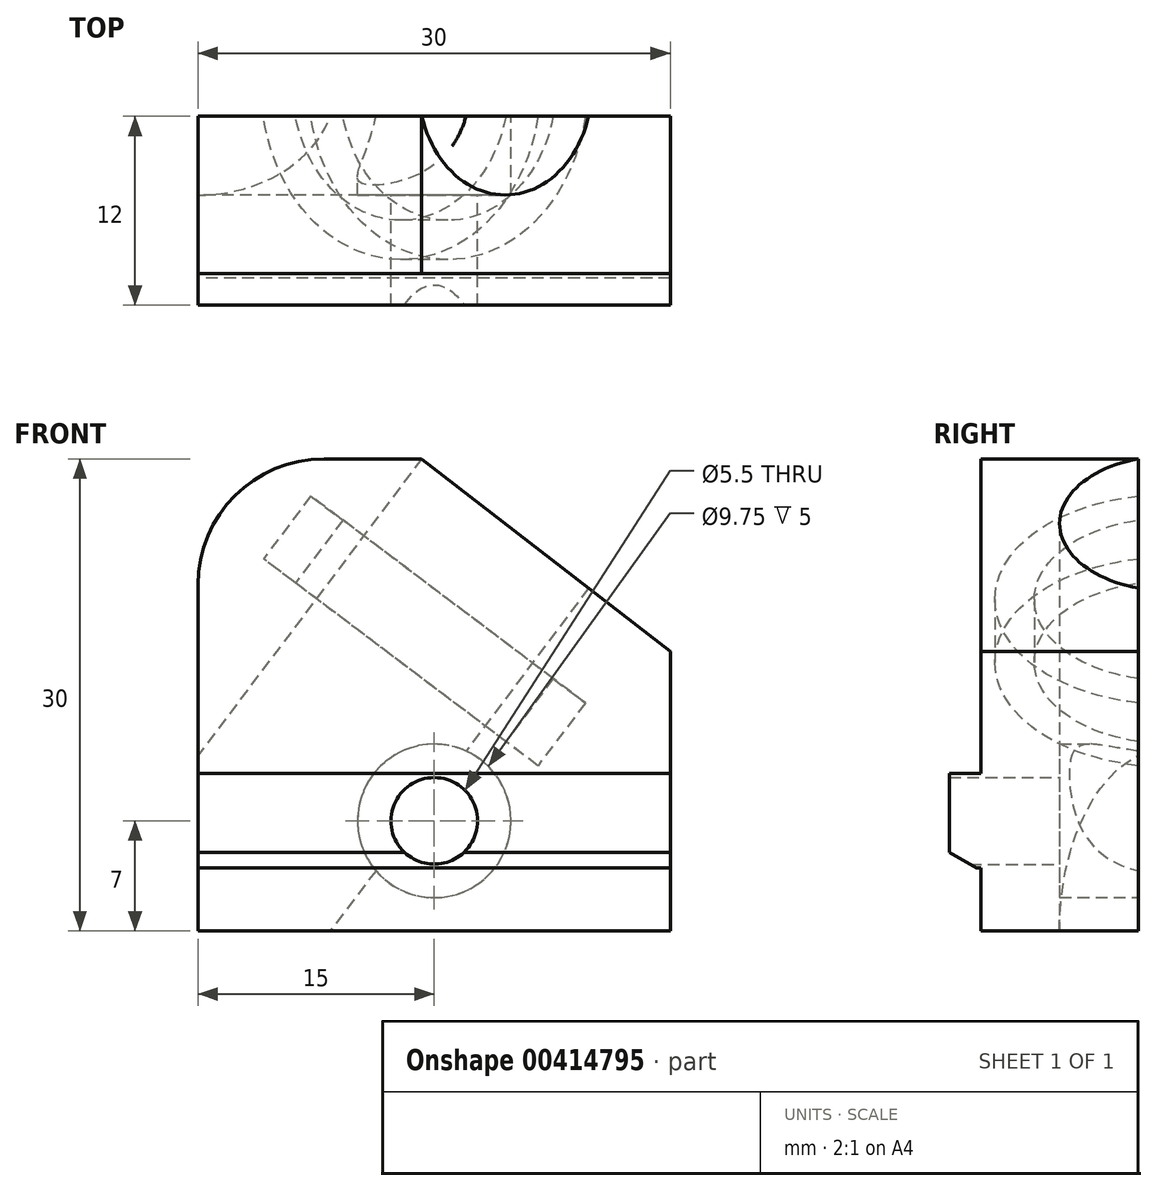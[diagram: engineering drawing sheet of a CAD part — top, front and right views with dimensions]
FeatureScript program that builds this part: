
annotation { "Feature Type Name" : "Feature", "Feature Type Description" : "" }
export const myFeature = defineFeature(function(context is Context, id is Id, definition is map)
    precondition{}
    {
        {
            var Q0;
            Q0=qCreatedBy(makeId("Top.planeOp"),FACE);
            var sketch = newSketch(context, id + "F0", { "sketchPlane" : qUnion([Q0])});
            skLineSegment(sketch, "E0.bottom", {"start": v(-15, 0) * mm, "end": v(15, 0) * mm});
            skLineSegment(sketch, "E0.top", {"start": v(-15, 10) * mm, "end": v(15, 10) * mm});
            skLineSegment(sketch, "E0.left", {"start": v(-15, 0) * mm, "end": v(-15, 10) * mm});
            skLineSegment(sketch, "E0.right", {"start": v(15, 0) * mm, "end": v(15, 10) * mm});
            skSolve(sketch);
        }
        {
            var Q0;
            Q0=makeQuery(id+"F0.imprint","IMPRINT",FACE,{"disambiguationData":[TD([[makeQuery(id+"F0.imprint","IMPRINT",EDGE,{"derivedFrom":sQuery(id+"F0.wireOp",EDGE,"E0.bottom")}),1.0]])]});
            extrude(context, id + "F1", {"entities" : qUnion([Q0]), "depth" : 30 * mm});
        }
        {
            var Q0;
            Q0=qCreatedBy(makeId("Front.planeOp"),FACE);
            cPlane(context, id + "F2", {"entities" : qUnion([Q0]), "cplaneType" : CPlaneType.OFFSET, "offset" : 12 * mm, "oppositeDirection" : true, "width" : 150 * mm, "height" : 150 * mm});
        }
        {
            var Q0;
            Q0=qCreatedBy(id+"F2.planeOp",FACE);
            var sketch = newSketch(context, id + "F3", { "sketchPlane" : qUnion([Q0])});
            skLineSegment(sketch, "E1", {"start": v(7.99, 30.5) * mm, "end": v(-17.36, -3.13) * mm, "construction": true});
            skLineSegment(sketch, "E2", {"start": v(11.35, 34.96) * mm, "end": v(16.94, 30.75) * mm});
            skLineSegment(sketch, "E3", {"start": v(16.94, 30.75) * mm, "end": v(-9.98, -4.96) * mm});
            skLineSegment(sketch, "E4", {"start": v(-9.98, -4.96) * mm, "end": v(-15.57, -0.75) * mm});
            skLineSegment(sketch, "E5", {"start": v(11.35, 34.96) * mm, "end": v(-15.57, -0.75) * mm});
            skLineSegment(sketch, "E6", {"start": v(7.74, 15.9) * mm, "end": v(4.74, 11.9) * mm});
            skLineSegment(sketch, "E7", {"start": v(4.74, 11.9) * mm, "end": v(6.73, 10.4) * mm});
            skLineSegment(sketch, "E8", {"start": v(6.73, 10.4) * mm, "end": v(9.74, 14.39) * mm});
            skLineSegment(sketch, "E9", {"start": v(9.74, 14.39) * mm, "end": v(7.74, 15.9) * mm});
            skSolve(sketch);
        }
        {
            var Q0;
            Q0=makeQuery(id+"F3.imprint","IMPRINT",FACE,{"disambiguationData":[TD([[makeQuery(id+"F3.imprint","IMPRINT",EDGE,{"derivedFrom":sQuery(id+"F3.wireOp",EDGE,"E2")}),-1.0]])]});
            var Q1;
            Q1=makeQuery(id+"F3.imprint","IMPRINT",FACE,{"disambiguationData":[TD([[makeQuery(id+"F3.imprint","IMPRINT",EDGE,{"derivedFrom":sQuery(id+"F3.wireOp",EDGE,"E6")}),1.0]])]});
            var Q2;
            Q2=sQuery(id+"F3.wireOp",EDGE,"E5");
            revolve(context, id + "F4", {"operationType" : NewBodyOperationType.REMOVE, "entities" : qUnion([Q0, Q1]), "axis" : qUnion([Q2]), "revolveType" : RevolveType.FULL, "oppositeDirection" : true});
        }
        {
            var Q0;
            Q0=qCreatedBy(id+"F2.planeOp",FACE);
            var sketch = newSketch(context, id + "F5", { "sketchPlane" : qUnion([Q0])});
            skLineSegment(sketch, "E10", {"start": v(23.6, 11.1) * mm, "end": v(-9.67, 36.88) * mm});
            skLineSegment(sketch, "E11", {"start": v(-9.67, 36.88) * mm, "end": v(-29.6, 11.17) * mm});
            skLineSegment(sketch, "E12", {"start": v(-29.6, 11.17) * mm, "end": v(3.67, -14.61) * mm});
            skLineSegment(sketch, "E13", {"start": v(3.67, -14.61) * mm, "end": v(23.6, 11.1) * mm});
            skSolve(sketch);
        }
        {
            var Q0;
            Q0=makeQuery(id+"F5.imprint","IMPRINT",FACE,{"disambiguationData":[TD([[makeQuery(id+"F5.imprint","IMPRINT",EDGE,{"derivedFrom":sQuery(id+"F5.wireOp",EDGE,"E10")}),1.0]])]});
            extrude(context, id + "F6", {"entities" : qUnion([Q0]), "operationType" : NewBodyOperationType.INTERSECT, "depth" : 25 * mm});
        }
        {
            var Q0;
            Q0=makeQuery(id+"F1.opExtrude","CAP_EDGE",EDGE,{"disambiguationData":[OSD([sQuery(id+"F0.wireOp",EDGE,"E0.left")])],"isStart":false});
            var Q1;
            Q1=makeQuery(id+"F6.boolean.opBoolean","INTERSECT",EDGE,{"derivedFrom":[makeQuery(id+"F1.opExtrude","SWEPT_FACE",FACE,{"disambiguationData":[OSD([sQuery(id+"F0.wireOp",EDGE,"E0.right")])]}),makeQuery(id+"F6.boolean.toolComplement.opBoolean","COPY",FACE,{"derivedFrom":makeQuery(id+"F6.opExtrude","SWEPT_FACE",FACE,{"disambiguationData":[OSD([sQuery(id+"F5.wireOp",EDGE,"E10")])]})})]});
            fillet(context, id + "F7", {"entities" : qUnion([Q0, Q1]), "radius" : 8 * mm, "tangentPropagation" : true, "allowEdgeOverflow" : false});
        }
        {
            var Q0;
            Q0=makeQuery(id+"F1.opExtrude","SWEPT_FACE",FACE,{"disambiguationData":[OSD([sQuery(id+"F0.wireOp",EDGE,"E0.bottom")])]});
            var sketch = newSketch(context, id + "F8", { "sketchPlane" : qUnion([Q0])});
            skLineSegment(sketch, "E14.bottom", {"start": v(-15, 4) * mm, "end": v(15, 4) * mm});
            skLineSegment(sketch, "E14.top", {"start": v(-15, 10) * mm, "end": v(15, 10) * mm});
            skLineSegment(sketch, "E14.left", {"start": v(-15, 4) * mm, "end": v(-15, 10) * mm});
            skLineSegment(sketch, "E14.right", {"start": v(15, 4) * mm, "end": v(15, 10) * mm});
            skSolve(sketch);
        }
        {
            var Q0;
            Q0=makeQuery(id+"F8.imprint","IMPRINT",FACE,{"disambiguationData":[TD([[makeQuery(id+"F8.imprint","IMPRINT",EDGE,{"derivedFrom":sQuery(id+"F8.wireOp",EDGE,"E14.bottom")}),1.0]])]});
            extrude(context, id + "F9", {"entities" : qUnion([Q0]), "operationType" : NewBodyOperationType.ADD, "depth" : 2 * mm});
        }
        {
            var Q0;
            {var subQ0=sQuery(id+"F0.wireOp",EDGE,"E0.right");var subQ1=sQuery(id+"F0.wireOp",EDGE,"E0.top");Q0=makeQuery(id+"F4.boolean.opBoolean","SPLIT",FACE,{"disambiguationData":[TD([makeQuery(id+"F1.opExtrude","SWEPT_FACE",FACE,{"disambiguationData":[OSD([subQ0])]})])],"derivedFrom":makeQuery(id+"F1.opExtrude","SWEPT_FACE",FACE,{"disambiguationData":[OSD([subQ1])]})});}
            var sketch = newSketch(context, id + "F10", { "sketchPlane" : qUnion([Q0])});
            skLineSegment(sketch, "E15", {"start": v(-15, 4) * mm, "end": v(15, 10) * mm, "construction": true});
            skPoint(sketch, "E16", {"position": v(0, 7) * mm});
            skSolve(sketch);
        }
        {
            var Q0;
            Q0=sQuery(id+"F10.wireOp",VERTEX,"E16");
            var Q1;
            Q1=makeQuery(id+"F1.opExtrude","SWEPT_BODY",BODY,{"disambiguationData":[OSD([sQuery(id+"F0.wireOp",EDGE,"E0.bottom"),sQuery(id+"F0.wireOp",EDGE,"E0.top"),sQuery(id+"F0.wireOp",EDGE,"E0.left"),sQuery(id+"F0.wireOp",EDGE,"E0.right")])]});
            hole(context, id + "F11", {"style" : HoleStyle.C_BORE, "endStyle" : HoleEndStyle.BLIND, "holeDiameter" : 5.5 * mm, "cBoreDiameter" : 9.75 * mm, "cBoreDepth" : 5 * mm, "holeDepth" : 100 * mm, "isTappedThrough" : true, "tappedDepth" : 15 * mm, "tapClearance" : 0, "startFromSketch" : true, "locations" : qUnion([Q0]), "scope" : qUnion([Q1])});
        }
        {
            var Q0;
            Q0=makeQuery(id+"F9.opExtrude","CAP_FACE",FACE,{"disambiguationData":[OSD([sQuery(id+"F8.wireOp",EDGE,"E14.bottom"),sQuery(id+"F8.wireOp",EDGE,"E14.top"),sQuery(id+"F8.wireOp",EDGE,"E14.left"),sQuery(id+"F8.wireOp",EDGE,"E14.right")])],"isStart":false});
            var sketch = newSketch(context, id + "F12", { "sketchPlane" : qUnion([Q0])});
            skCircle(sketch, "E17", {"center": v(0, 7) * mm, "radius": 6.3 * mm});
            skSolve(sketch);
        }
        {
            var Q0;
            {var subQ0=sQuery(id+"F12.wireOp",EDGE,"E17");var subQ5=sQuery(id+"F8.wireOp",EDGE,"E14.top");var subQ6=makeQuery(id+"F9.opExtrude","CAP_EDGE",EDGE,{"disambiguationData":[OSD([subQ5])],"isStart":false});var subQ8=makeQuery(id+"F12.imprint","INTERSECT",VERTEX,{"disambiguationData":[OD(0.0)],"derivedFrom":[subQ6,subQ0]});Q0=makeQuery(id+"F12.imprint","IMPRINT",FACE,{"disambiguationData":[TD([[makeQuery(id+"F12.imprint","IMPRINT",EDGE,{"disambiguationData":[TD([[subQ8,-1.0]])],"derivedFrom":subQ0}),1.0]])]});}
            extrude(context, id + "F13", {"entities" : qUnion([Q0]), "operationType" : NewBodyOperationType.REMOVE, "oppositeDirection" : true, "depth" : 2 * mm});
        }
        {
            var Q0;
            {var subQ1=sQuery(id+"F8.wireOp",EDGE,"E14.bottom");var subQ4=makeQuery(id+"F9.opExtrude","CAP_EDGE",EDGE,{"disambiguationData":[OSD([subQ1])],"isStart":false});Q0=makeQuery(id+"F13.boolean.opBoolean","SPLIT",EDGE,{"disambiguationData":[TD([makeQuery(id+"F1.opExtrude","SWEPT_FACE",FACE,{"disambiguationData":[OSD([sQuery(id+"F0.wireOp",EDGE,"E0.right")])]})])],"derivedFrom":subQ4});}
            var Q1;
            {var subQ2=sQuery(id+"F8.wireOp",EDGE,"E14.bottom");var subQ4=makeQuery(id+"F9.opExtrude","CAP_EDGE",EDGE,{"disambiguationData":[OSD([subQ2])],"isStart":false});Q1=makeQuery(id+"F13.boolean.opBoolean","SPLIT",EDGE,{"disambiguationData":[TD([makeQuery(id+"F1.opExtrude","SWEPT_FACE",FACE,{"disambiguationData":[OSD([sQuery(id+"F0.wireOp",EDGE,"E0.left")])]})])],"derivedFrom":subQ4});}
            chamfer(context, id + "F14", {"entities" : qUnion([Q0, Q1]), "chamferType" : ChamferType.OFFSET_ANGLE, "width" : 1 * mm, "oppositeDirection" : false, "angle" : 60 * degree, "tangentPropagation" : true});
        }
    });
